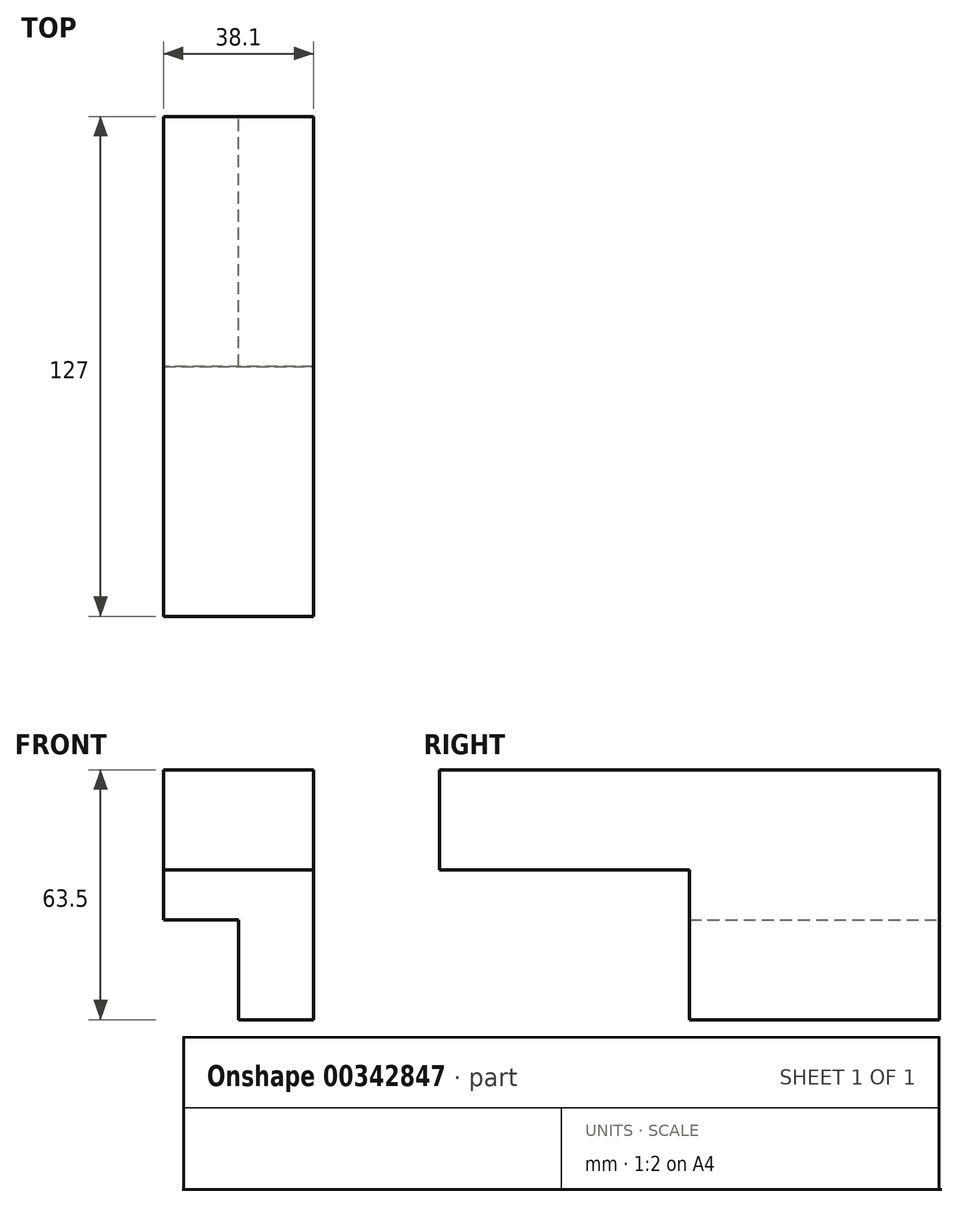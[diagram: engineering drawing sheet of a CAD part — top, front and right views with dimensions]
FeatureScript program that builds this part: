
annotation { "Feature Type Name" : "Feature", "Feature Type Description" : "" }
export const myFeature = defineFeature(function(context is Context, id is Id, definition is map)
    precondition{}
    {
        {
            var Q0;
            Q0=qCreatedBy(makeId("Front.planeOp"),FACE);
            var sketch = newSketch(context, id + "F0", { "sketchPlane" : qUnion([Q0])});
            skLineSegment(sketch, "E0.bottom", {"start": v(0, -31.75) * mm, "end": v(19.05, -31.75) * mm});
            skLineSegment(sketch, "E0.top", {"start": v(-19.05, 31.75) * mm, "end": v(19.05, 31.75) * mm});
            skLineSegment(sketch, "E0.left", {"start": v(-19.05, -6.35) * mm, "end": v(-19.05, 31.75) * mm});
            skLineSegment(sketch, "E0.right", {"start": v(19.05, -31.75) * mm, "end": v(19.05, 31.75) * mm});
            skPoint(sketch, "E0.middle", {"position": v(0, 0) * mm});
            skLineSegment(sketch, "E1", {"start": v(19.05, 31.75) * mm, "end": v(19.05, 6.35) * mm});
            skLineSegment(sketch, "E2", {"start": v(19.05, -31.75) * mm, "end": v(19.05, -6.35) * mm});
            skLineSegment(sketch, "E3", {"start": v(19.05, 6.35) * mm, "end": v(-19.05, 6.35) * mm});
            skLineSegment(sketch, "E4", {"start": v(-19.05, -6.35) * mm, "end": v(0, -6.35) * mm});
            skLineSegment(sketch, "E5", {"start": v(0, -6.35) * mm, "end": v(0, -31.75) * mm});
            skPoint(sketch, "E6.orphan", {"position": v(-19.05, -31.75) * mm});
            skSolve(sketch);
        }
        {
            var Q0;
            Q0=makeQuery(id+"F0.imprint","IMPRINT",FACE,{"disambiguationData":[TD([[makeQuery(id+"F0.imprint","IMPRINT",EDGE,{"derivedFrom":sQuery(id+"F0.wireOp",EDGE,"E0.right")}),1.0]])]});
            extrude(context, id + "F1", {"entities" : qUnion([Q0]), "depth" : 127 * mm});
        }
        {
            var Q0;
            Q0 = qSketchRegion(id + "F0", true);
            extrude(context, id + "F2", {"entities" : qUnion([Q0]), "operationType" : NewBodyOperationType.ADD, "depth" : 63.5 * mm});
        }
    });
